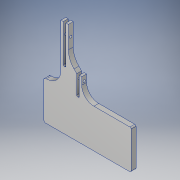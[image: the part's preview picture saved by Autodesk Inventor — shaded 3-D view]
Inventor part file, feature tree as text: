
AUTODESK INVENTOR PART (.ipt)
format: ipt  version: 2017 (Build 210142000, 142)  size: 239,104 bytes
history: native  units: in
note: dims shown in document units (in); Inventor stores cm internally (conversion verified against a paired STEP export)
features: sketch x15, extrude x12, fillet x5
ambient origin geometry x8: Origin, YZ Plane, XZ Plane, XY Plane, X Axis, Y Axis, Z Axis, Center Point
bodies: Solid1 (feature_tree)
feature tree (32):
  extrude  "Extrusion1"  Depth=2.0in
  sketch  "Sketch2"  dims[d3=4.5in d4=0.125in d5=0.0in]
  extrude  "Extrusion2"  Depth=0.125in TaperAngle=0.0deg
  extrude  "Extrusion3"  Depth=0.066in
  extrude  "Extrusion4"  Depth=0.25in
  extrude  "Extrusion5"  Depth=0.125in TaperAngle=0.0deg
  extrude  "Extrusion6"  Depth=3.0in TaperAngle=0.0deg
  sketch  "Sketch6"  dims[d14=3.0in d15=0.0in d16=3.0in d17=0.0in]
  sketch  "Sketch7"  dims[d18=0.75in d19=0.125in]
  sketch  "Sketch8"  dims[d20=2.0in d21=0.0in d22=1.64in]
  sketch  "Sketch9"  dims[d23=0.125in d24=2.0in d25=0.0in]
  extrude  "Extrusion11"  Depth=0.125in
  extrude  "Extrusion12"  Depth=2.0in
  extrude  "Extrusion13"  Depth=2.0in TaperAngle=0.0deg
  extrude  "Extrusion14"  Depth=0.125in
  extrude  "Extrusion15"  Depth=0.125in
  extrude  "Extrusion16"  Depth=0.125in
  fillet  "Fillet1"  Radius=0.25in
  fillet  "Fillet3"  Radius=0.067in
  fillet  "Fillet4"  Radius=0.125in
  fillet  "Fillet5"  Radius=0.25in
  fillet  "Fillet6"  Radius=0.125in
  sketch  "Sketch1"  dims[d1=4.5in d2=2.0in]
  sketch  "Sketch3"  dims[d7=0.066in d8=0.066in]
  sketch  "Sketch4"  dims[d9=0.125in d10=0.25in]
  sketch  "Sketch5"  dims[d11=0.125in d12=0.125in d13=0.0in]
  sketch  "Sketch12"  dims[d30=0.125in d34=0.125in]
  sketch  "Sketch13"  dims[d35=0.132in d36=0.125in]
  sketch  "Sketch14"  dims[d44=0.067in d45=0.125in d46=0.25in d47=0.0in d48=0.067in d49=0.125in d50=0.25in d51=0.0in d52=0.125in]
  sketch  "Sketch15"  dims[d55=0.25in d56=0.0in]
  sketch  "Sketch16"  dims[d57=2.0in d58=0.0in]
  sketch  "Sketch17"  dims[d59=0.25in d60=0.0in d61=0.5in d62=0.0in d63=0.0625in d65=1.0in d67=0.625in d68=0.0625in d69=0.75in]
